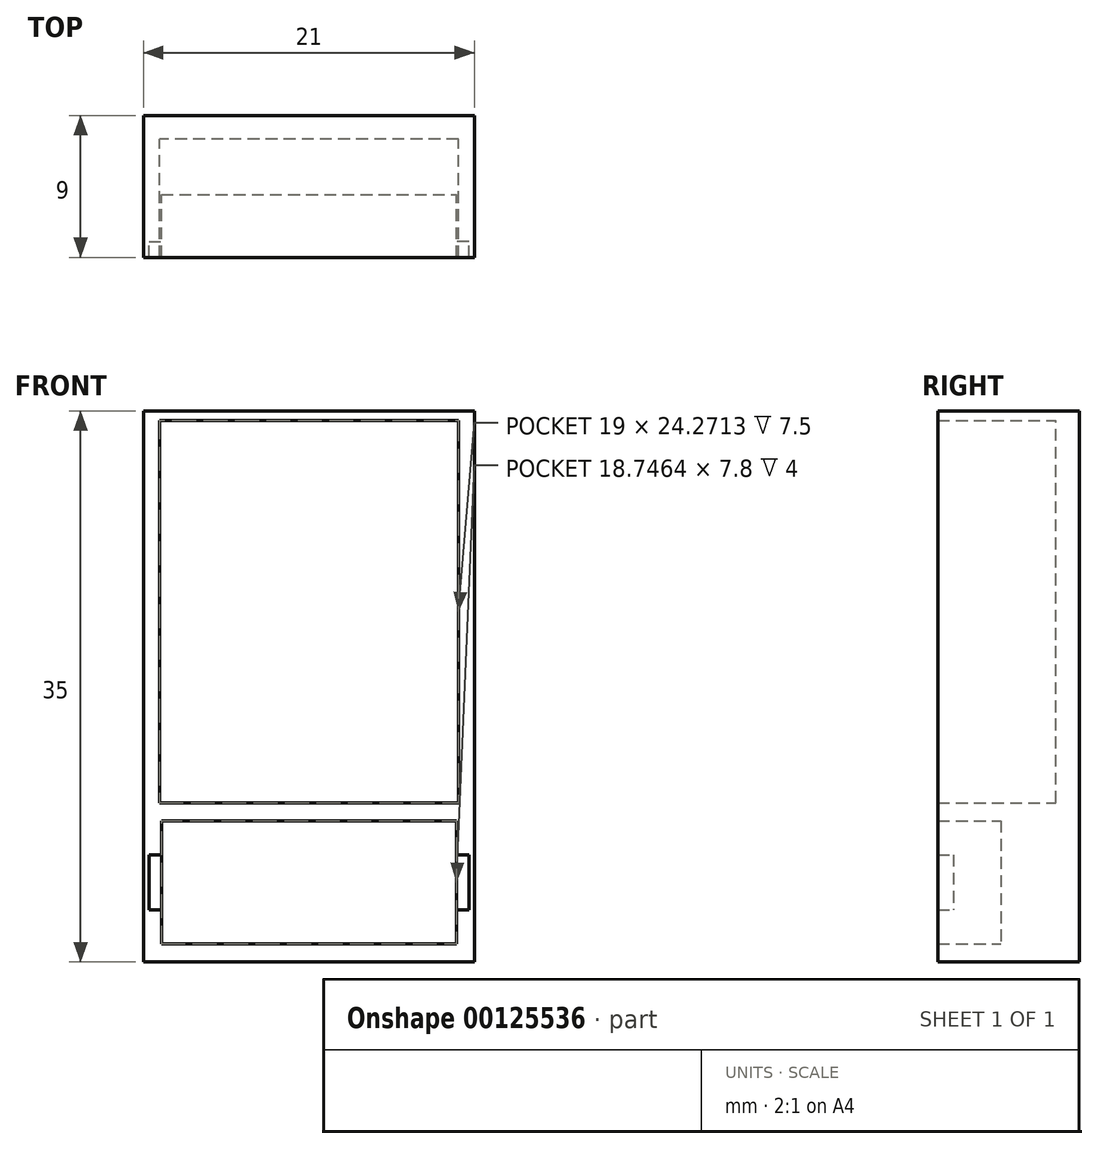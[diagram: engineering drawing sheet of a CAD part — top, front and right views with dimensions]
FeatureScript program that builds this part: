
annotation { "Feature Type Name" : "Feature", "Feature Type Description" : "" }
export const myFeature = defineFeature(function(context is Context, id is Id, definition is map)
    precondition{}
    {
        {
            var Q0;
            Q0=qCreatedBy(makeId("Front.planeOp"),FACE);
            var sketch = newSketch(context, id + "F0", { "sketchPlane" : qUnion([Q0])});
            skLineSegment(sketch, "E0.bottom", {"start": v(10.5, -17.5) * mm, "end": v(-10.5, -17.5) * mm});
            skLineSegment(sketch, "E0.top", {"start": v(10.5, 17.5) * mm, "end": v(-10.5, 17.5) * mm});
            skLineSegment(sketch, "E0.left", {"start": v(10.5, -17.5) * mm, "end": v(10.5, 17.5) * mm});
            skLineSegment(sketch, "E0.right", {"start": v(-10.5, -17.5) * mm, "end": v(-10.5, 17.5) * mm});
            skPoint(sketch, "E0.middle", {"position": v(0, 0) * mm});
            skLineSegment(sketch, "E1.bottom", {"start": v(9.5, -7.4) * mm, "end": v(-9.5, -7.4) * mm});
            skLineSegment(sketch, "E1.top", {"start": v(9.5, 16.88) * mm, "end": v(-9.5, 16.88) * mm});
            skLineSegment(sketch, "E1.left", {"start": v(9.5, -7.4) * mm, "end": v(9.5, 16.88) * mm});
            skLineSegment(sketch, "E1.right", {"start": v(-9.5, -7.4) * mm, "end": v(-9.5, 16.88) * mm});
            skPoint(sketch, "E1.middle", {"position": v(0, 4.74) * mm});
            skLineSegment(sketch, "E2.bottom", {"start": v(-9.37, -8.54) * mm, "end": v(9.37, -8.54) * mm});
            skLineSegment(sketch, "E2.top", {"start": v(-9.37, -16.34) * mm, "end": v(9.37, -16.34) * mm});
            skLineSegment(sketch, "E2.left", {"start": v(-9.37, -8.54) * mm, "end": v(-9.37, -16.34) * mm});
            skLineSegment(sketch, "E2.right", {"start": v(9.37, -8.54) * mm, "end": v(9.37, -16.34) * mm});
            skPoint(sketch, "E2.middle", {"position": v(0, -12.44) * mm});
            skLineSegment(sketch, "E3.bottom", {"start": v(10.17, -10.7) * mm, "end": v(9.37, -10.7) * mm});
            skLineSegment(sketch, "E3.top", {"start": v(10.17, -14.2) * mm, "end": v(9.37, -14.2) * mm});
            skLineSegment(sketch, "E3.left", {"start": v(10.17, -10.7) * mm, "end": v(10.17, -14.2) * mm});
            skPoint(sketch, "E3.middle", {"position": v(9.37, -12.44) * mm});
            skLineSegment(sketch, "E4.MirrorCS", {"start": v(-10.17, -14.2) * mm, "end": v(-9.37, -14.2) * mm});
            skPoint(sketch, "E5.MirrorP", {"position": v(-9.37, -12.44) * mm});
            skLineSegment(sketch, "E6.MirrorCS", {"start": v(-10.17, -10.7) * mm, "end": v(-10.17, -14.2) * mm});
            skLineSegment(sketch, "E7.MirrorCS", {"start": v(-10.17, -10.7) * mm, "end": v(-9.37, -10.7) * mm});
            skPoint(sketch, "E3.right.start.orphan", {"position": v(8.58, -10.7) * mm});
            skPoint(sketch, "E8.orphan", {"position": v(8.58, -14.2) * mm});
            skPoint(sketch, "E9.orphan", {"position": v(-8.58, -10.7) * mm});
            skPoint(sketch, "E10.orphan", {"position": v(-8.58, -14.2) * mm});
            skSolve(sketch);
        }
        {
            var Q0;
            Q0=makeQuery(id+"F0.imprint","IMPRINT",FACE,{"disambiguationData":[TD([[makeQuery(id+"F0.imprint","IMPRINT",EDGE,{"derivedFrom":sQuery(id+"F0.wireOp",EDGE,"E0.bottom")}),-1.0]])]});
            extrude(context, id + "F1", {"entities" : qUnion([Q0]), "depth" : 9 * mm});
        }
        {
            var Q0;
            Q0=makeQuery(id+"F0.imprint","IMPRINT",FACE,{"disambiguationData":[TD([[makeQuery(id+"F0.imprint","IMPRINT",EDGE,{"derivedFrom":sQuery(id+"F0.wireOp",EDGE,"E1.bottom")}),-1.0]])]});
            extrude(context, id + "F2", {"entities" : qUnion([Q0]), "operationType" : NewBodyOperationType.ADD, "depth" : 1.5 * mm});
        }
        {
            var Q0;
            Q0=makeQuery(id+"F0.imprint","IMPRINT",FACE,{"disambiguationData":[TD([[makeQuery(id+"F0.imprint","IMPRINT",EDGE,{"derivedFrom":sQuery(id+"F0.wireOp",EDGE,"E2.bottom")}),-1.0]])]});
            extrude(context, id + "F3", {"entities" : qUnion([Q0]), "operationType" : NewBodyOperationType.ADD, "depth" : 5 * mm});
        }
        {
            var Q0;
            {var subQ5=sQuery(id+"F0.wireOp",EDGE,"E3.left");Q0=makeQuery(id+"F0.imprint","IMPRINT",FACE,{"disambiguationData":[TD([[makeQuery(id+"F0.imprint","IMPRINT",EDGE,{"derivedFrom":subQ5}),-1.0]])]});}
            var Q1;
            {var subQ0=sQuery(id+"F0.wireOp",EDGE,"E6.MirrorCS");Q1=makeQuery(id+"F0.imprint","IMPRINT",FACE,{"disambiguationData":[TD([[makeQuery(id+"F0.imprint","IMPRINT",EDGE,{"derivedFrom":subQ0}),1.0]])]});}
            var Q2;
            {var subQ5=sQuery(id+"F0.wireOp",EDGE,"E3.right");Q2=makeQuery(id+"F0.imprint","IMPRINT",FACE,{"disambiguationData":[TD([[makeQuery(id+"F0.imprint","IMPRINT",EDGE,{"derivedFrom":subQ5}),1.0]])]});}
            var Q3;
            {var subQ0=sQuery(id+"F0.wireOp",EDGE,"3db82735-4d16-4ada-ae46-28c476be95662.MirrorCS");Q3=makeQuery(id+"F0.imprint","IMPRINT",FACE,{"disambiguationData":[TD([[makeQuery(id+"F0.imprint","IMPRINT",EDGE,{"derivedFrom":subQ0}),-1.0]])]});}
            extrude(context, id + "F4", {"entities" : qUnion([Q0, Q1, Q2, Q3]), "operationType" : NewBodyOperationType.ADD, "depth" : 8 * mm});
        }
    });
